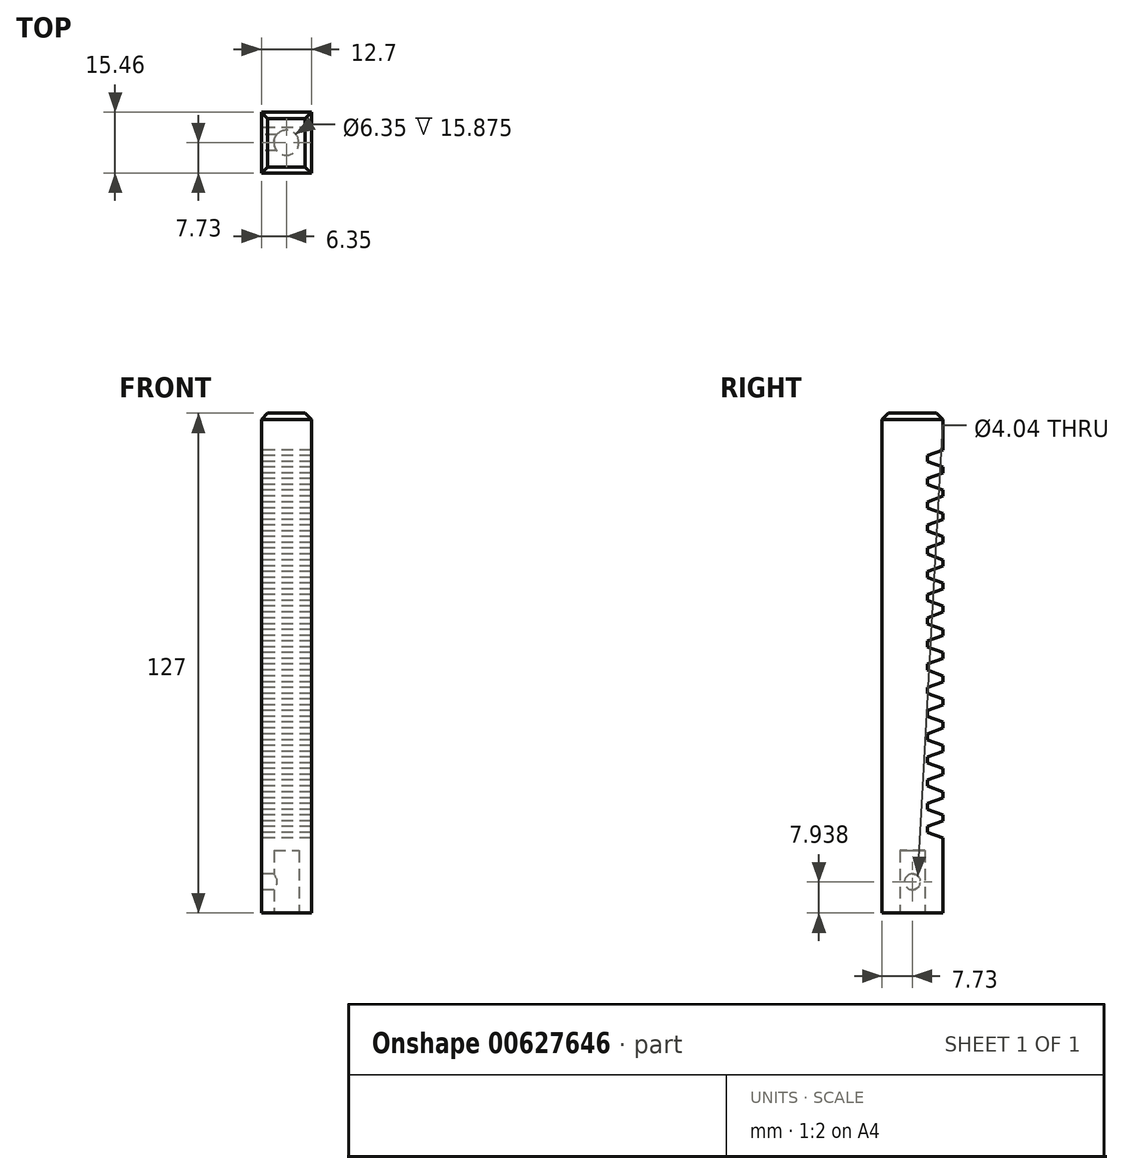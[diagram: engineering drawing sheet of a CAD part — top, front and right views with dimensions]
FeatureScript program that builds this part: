
annotation { "Feature Type Name" : "Feature", "Feature Type Description" : "" }
export const myFeature = defineFeature(function(context is Context, id is Id, definition is map)
    precondition{}
    {
        {
            var Q0;
            Q0=qCreatedBy(makeId("Right.planeOp"),FACE);
            var sketch = newSketch(context, id + "F0", { "sketchPlane" : qUnion([Q0])});
            skLineSegment(sketch, "E0.bottom", {"start": v(-7.73, -63.5) * mm, "end": v(7.73, -63.5) * mm});
            skLineSegment(sketch, "E0.top", {"start": v(-7.73, 63.5) * mm, "end": v(7.73, 63.5) * mm});
            skLineSegment(sketch, "E0.left", {"start": v(-7.73, -63.5) * mm, "end": v(-7.73, 63.5) * mm});
            skLineSegment(sketch, "E0.right", {"start": v(7.73, -63.5) * mm, "end": v(7.73, 63.5) * mm});
            skPoint(sketch, "E0.middle", {"position": v(0, 0) * mm});
            skSolve(sketch);
        }
        {
            var Q0;
            Q0 = qSketchRegion(id + "F0", true);
            extrude(context, id + "F1", {"entities" : qUnion([Q0]), "depth" : 12.7 * mm, "offsetDistance" : 25.4 * mm});
        }
        {
            var Q0;
            Q0=qCreatedBy(makeId("Right.planeOp"),FACE);
            var sketch = newSketch(context, id + "F2", { "sketchPlane" : qUnion([Q0])});
            skCircle(sketch, "E1.MirrorC", {"center": v(0, -55.56) * mm, "radius": 2.02 * mm});
            skSolve(sketch);
        }
        {
            var Q0;
            Q0 = qSketchRegion(id + "F2", true);
            extrude(context, id + "F3", {"entities" : qUnion([Q0]), "operationType" : NewBodyOperationType.REMOVE, "depth" : 6.35 * mm, "offsetDistance" : 25.4 * mm});
        }
        {
            var Q0;
            Q0=makeQuery(id+"F1.opExtrude","SWEPT_FACE",FACE,{"disambiguationData":[OSD([sQuery(id+"F0.wireOp",EDGE,"E0.bottom")])]});
            var sketch = newSketch(context, id + "F4", { "sketchPlane" : qUnion([Q0])});
            skCircle(sketch, "E2", {"center": v(6.35, 0) * mm, "radius": 3.18 * mm});
            skPoint(sketch, "E2.centerSnap0", {"position": v(6.35, 7.73) * mm});
            skSolve(sketch);
        }
        {
            var Q0;
            Q0 = qSketchRegion(id + "F4", true);
            extrude(context, id + "F5", {"entities" : qUnion([Q0]), "operationType" : NewBodyOperationType.REMOVE, "oppositeDirection" : true, "depth" : 15.88 * mm, "offsetDistance" : 25.4 * mm});
        }
        {
            var Q0;
            Q0=makeQuery(id+"F1.opExtrude","SWEPT_FACE",FACE,{"disambiguationData":[OSD([sQuery(id+"F0.wireOp",EDGE,"E0.top")])]});
            chamfer(context, id + "F6", {"entities" : qUnion([Q0]), "width" : 1.6 * mm, "tangentPropagation" : true});
        }
        {
            var Q0;
            Q0=makeQuery(id+"F1.opExtrude","CAP_FACE",FACE,{"disambiguationData":[OSD([sQuery(id+"F0.wireOp",EDGE,"E0.bottom"),sQuery(id+"F0.wireOp",EDGE,"E0.top"),sQuery(id+"F0.wireOp",EDGE,"E0.left"),sQuery(id+"F0.wireOp",EDGE,"E0.right")])],"isStart":true});
            var sketch = newSketch(context, id + "F7", { "sketchPlane" : qUnion([Q0])});
            skLineSegment(sketch, "E3", {"start": v(-3.82, -41.5) * mm, "end": v(-7.73, -40.08) * mm});
            skLineSegment(sketch, "E4.MirrorCS", {"start": v(-3.82, -43.03) * mm, "end": v(-3.82, -41.5) * mm});
            skLineSegment(sketch, "E5.MirrorCS", {"start": v(-7.73, -44.45) * mm, "end": v(-3.82, -43.03) * mm});
            skLineSegment(sketch, "E6.0.1.0", {"start": v(-7.73, -38.56) * mm, "end": v(-3.82, -37.13) * mm});
            skLineSegment(sketch, "E6.0.1.1", {"start": v(-3.82, -37.13) * mm, "end": v(-3.82, -35.6) * mm});
            skLineSegment(sketch, "E6.0.1.2", {"start": v(-3.82, -35.6) * mm, "end": v(-7.73, -34.19) * mm});
            skLineSegment(sketch, "E6.0.2.0", {"start": v(-7.73, -32.66) * mm, "end": v(-3.82, -31.24) * mm});
            skLineSegment(sketch, "E6.0.2.1", {"start": v(-3.82, -31.24) * mm, "end": v(-3.82, -29.72) * mm});
            skLineSegment(sketch, "E6.0.2.2", {"start": v(-3.82, -29.72) * mm, "end": v(-7.73, -28.3) * mm});
            skLineSegment(sketch, "E6.0.3.0", {"start": v(-7.73, -26.77) * mm, "end": v(-3.82, -25.35) * mm});
            skLineSegment(sketch, "E6.0.3.1", {"start": v(-3.82, -25.35) * mm, "end": v(-3.82, -23.82) * mm});
            skLineSegment(sketch, "E6.0.3.2", {"start": v(-3.82, -23.82) * mm, "end": v(-7.73, -22.4) * mm});
            skLineSegment(sketch, "E6.0.4.0", {"start": v(-7.73, -20.88) * mm, "end": v(-3.82, -19.46) * mm});
            skLineSegment(sketch, "E6.0.4.1", {"start": v(-3.82, -19.46) * mm, "end": v(-3.82, -17.93) * mm});
            skLineSegment(sketch, "E6.0.4.2", {"start": v(-3.82, -17.93) * mm, "end": v(-7.73, -16.5) * mm});
            skLineSegment(sketch, "E6.0.5.0", {"start": v(-7.73, -14.99) * mm, "end": v(-3.82, -13.56) * mm});
            skLineSegment(sketch, "E6.0.5.1", {"start": v(-3.82, -13.56) * mm, "end": v(-3.82, -12.04) * mm});
            skLineSegment(sketch, "E6.0.5.2", {"start": v(-3.82, -12.04) * mm, "end": v(-7.73, -10.61) * mm});
            skLineSegment(sketch, "E6.0.6.0", {"start": v(-7.73, -9.1) * mm, "end": v(-3.82, -7.67) * mm});
            skLineSegment(sketch, "E6.0.6.1", {"start": v(-3.82, -7.67) * mm, "end": v(-3.82, -6.15) * mm});
            skLineSegment(sketch, "E6.0.6.2", {"start": v(-3.82, -6.15) * mm, "end": v(-7.73, -4.72) * mm});
            skLineSegment(sketch, "E6.0.7.0", {"start": v(-7.73, -3.2) * mm, "end": v(-3.82, -1.78) * mm});
            skLineSegment(sketch, "E6.0.7.1", {"start": v(-3.82, -1.78) * mm, "end": v(-3.82, -0.25) * mm});
            skLineSegment(sketch, "E6.0.7.2", {"start": v(-3.82, -0.25) * mm, "end": v(-7.73, 1.17) * mm});
            skLineSegment(sketch, "E6.0.8.0", {"start": v(-7.73, 2.7) * mm, "end": v(-3.82, 4.12) * mm});
            skLineSegment(sketch, "E6.0.8.1", {"start": v(-3.82, 4.12) * mm, "end": v(-3.82, 5.64) * mm});
            skLineSegment(sketch, "E6.0.8.2", {"start": v(-3.82, 5.64) * mm, "end": v(-7.73, 7.06) * mm});
            skLineSegment(sketch, "E6.0.9.0", {"start": v(-7.73, 8.59) * mm, "end": v(-3.82, 10) * mm});
            skLineSegment(sketch, "E6.0.9.1", {"start": v(-3.82, 10) * mm, "end": v(-3.82, 11.53) * mm});
            skLineSegment(sketch, "E6.0.9.2", {"start": v(-3.82, 11.53) * mm, "end": v(-7.73, 12.96) * mm});
            skLineSegment(sketch, "E6.0.10.0", {"start": v(-7.73, 14.48) * mm, "end": v(-3.82, 15.9) * mm});
            skLineSegment(sketch, "E6.0.10.1", {"start": v(-3.82, 15.9) * mm, "end": v(-3.82, 17.43) * mm});
            skLineSegment(sketch, "E6.0.10.2", {"start": v(-3.82, 17.43) * mm, "end": v(-7.73, 18.85) * mm});
            skLineSegment(sketch, "E6.0.11.0", {"start": v(-7.73, 20.37) * mm, "end": v(-3.82, 21.8) * mm});
            skLineSegment(sketch, "E6.0.11.1", {"start": v(-3.82, 21.8) * mm, "end": v(-3.82, 23.32) * mm});
            skLineSegment(sketch, "E6.0.11.2", {"start": v(-3.82, 23.32) * mm, "end": v(-7.73, 24.74) * mm});
            skLineSegment(sketch, "E6.0.12.0", {"start": v(-7.73, 26.26) * mm, "end": v(-3.82, 27.69) * mm});
            skLineSegment(sketch, "E6.0.12.1", {"start": v(-3.82, 27.69) * mm, "end": v(-3.82, 29.21) * mm});
            skLineSegment(sketch, "E6.0.12.2", {"start": v(-3.82, 29.21) * mm, "end": v(-7.73, 30.64) * mm});
            skLineSegment(sketch, "E6.0.13.0", {"start": v(-7.73, 32.16) * mm, "end": v(-3.82, 33.58) * mm});
            skLineSegment(sketch, "E6.0.13.1", {"start": v(-3.82, 33.58) * mm, "end": v(-3.82, 35.1) * mm});
            skLineSegment(sketch, "E6.0.13.2", {"start": v(-3.82, 35.1) * mm, "end": v(-7.73, 36.53) * mm});
            skLineSegment(sketch, "E6.0.14.0", {"start": v(-7.73, 38.05) * mm, "end": v(-3.82, 39.47) * mm});
            skLineSegment(sketch, "E6.0.14.1", {"start": v(-3.82, 39.47) * mm, "end": v(-3.82, 41) * mm});
            skLineSegment(sketch, "E6.0.14.2", {"start": v(-3.82, 41) * mm, "end": v(-7.73, 42.42) * mm});
            skLineSegment(sketch, "E6.0.15.0", {"start": v(-7.73, 43.94) * mm, "end": v(-3.82, 45.37) * mm});
            skLineSegment(sketch, "E6.0.15.1", {"start": v(-3.82, 45.37) * mm, "end": v(-3.82, 46.89) * mm});
            skLineSegment(sketch, "E6.0.15.2", {"start": v(-3.82, 46.89) * mm, "end": v(-7.73, 48.31) * mm});
            skLineSegment(sketch, "E6.0.16.0", {"start": v(-7.73, 49.83) * mm, "end": v(-3.82, 51.26) * mm});
            skLineSegment(sketch, "E6.0.16.1", {"start": v(-3.82, 51.26) * mm, "end": v(-3.82, 52.78) * mm});
            skLineSegment(sketch, "E6.0.16.2", {"start": v(-3.82, 52.78) * mm, "end": v(-7.73, 54.2) * mm});
            skLineSegment(sketch, "E6.direction1", {"start": v(-7.73, -44.45) * mm, "end": v(17.67, -44.45) * mm, "construction": true});
            skLineSegment(sketch, "E7", {"start": v(-7.73, 54.2) * mm, "end": v(-7.73, -44.45) * mm});
            skSolve(sketch);
        }
        {
            var Q0;
            Q0 = qSketchRegion(id + "F7", true);
            extrude(context, id + "F8", {"entities" : qUnion([Q0]), "operationType" : NewBodyOperationType.REMOVE, "oppositeDirection" : true, "depth" : 25.4 * mm, "offsetDistance" : 25.4 * mm});
        }
    });
